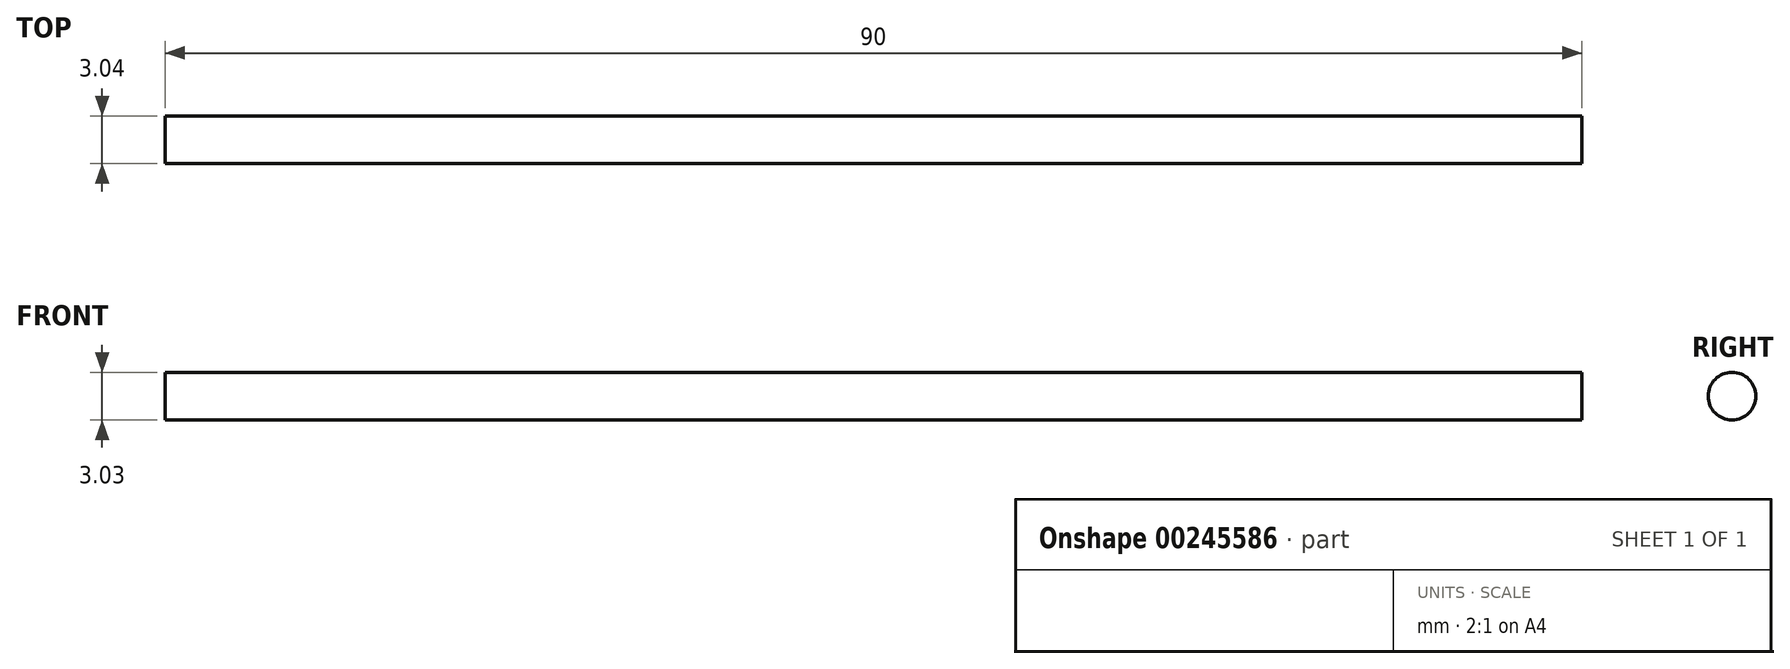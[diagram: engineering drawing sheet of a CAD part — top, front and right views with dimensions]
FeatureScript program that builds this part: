
annotation { "Feature Type Name" : "Feature", "Feature Type Description" : "" }
export const myFeature = defineFeature(function(context is Context, id is Id, definition is map)
    precondition{}
    {
        {
            var Q0;
            Q0=qCreatedBy(makeId("Right.planeOp"),FACE);
            var sketch = newSketch(context, id + "F0", { "sketchPlane" : qUnion([Q0])});
            skCircle(sketch, "E0", {"center": v(-3.5, 58.82) * mm, "radius": 1.52 * mm});
            skSolve(sketch);
        }
        {
            var Q0;
            Q0 = qSketchRegion(id + "F0", true);
            extrude(context, id + "F1", {"entities" : qUnion([Q0]), "depth" : 90 * mm});
        }
    });
